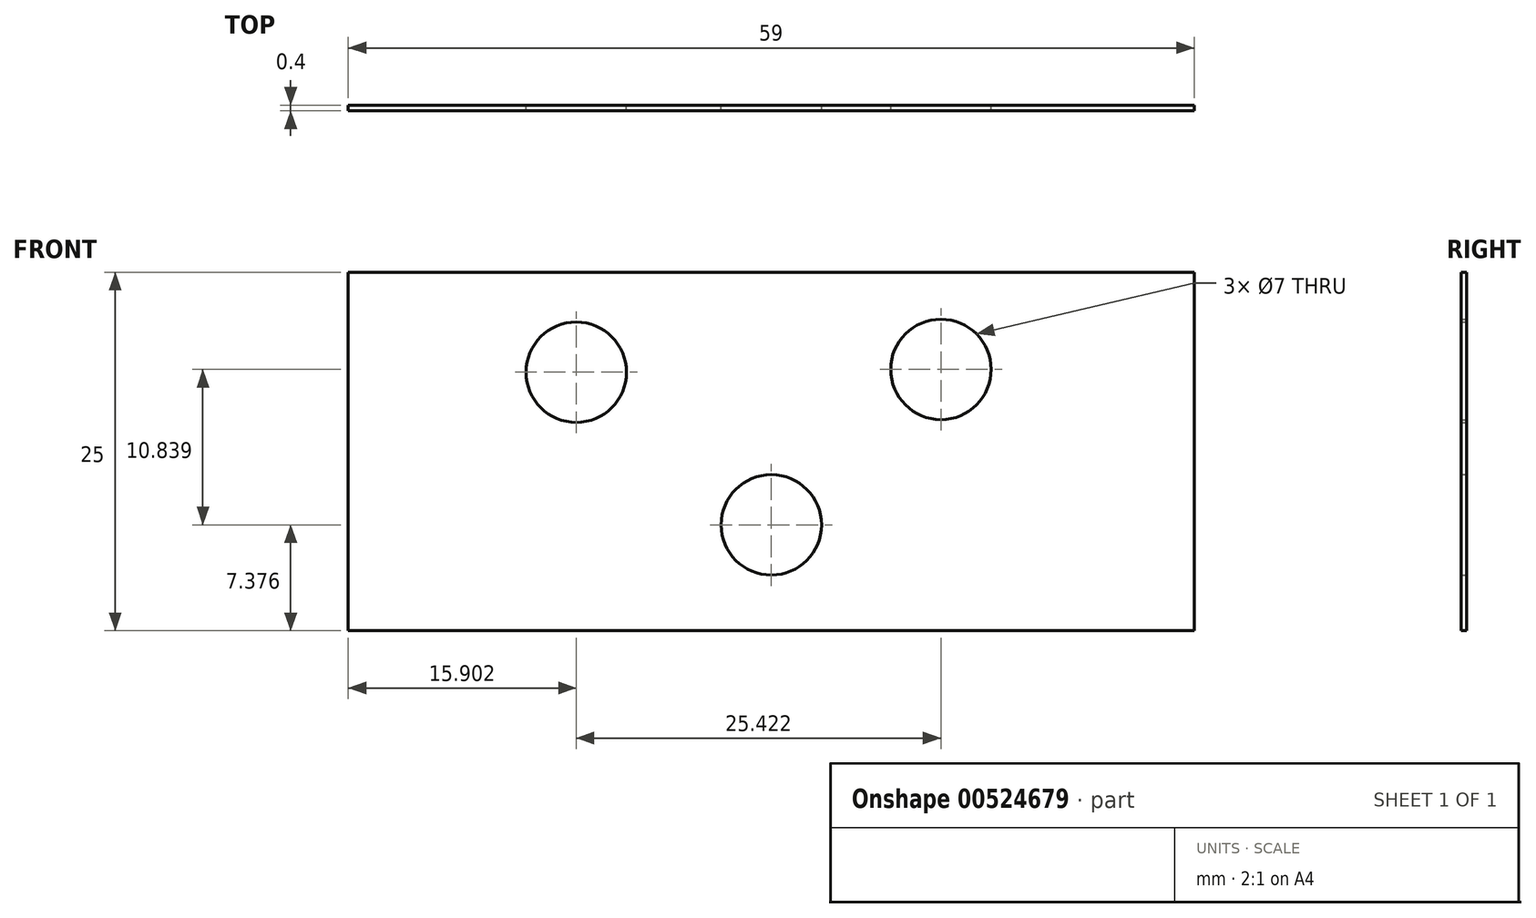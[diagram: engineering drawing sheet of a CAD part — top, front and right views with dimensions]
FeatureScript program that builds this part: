
annotation { "Feature Type Name" : "Feature", "Feature Type Description" : "" }
export const myFeature = defineFeature(function(context is Context, id is Id, definition is map)
    precondition{}
    {
        {
            var Q0;
            Q0=qCreatedBy(makeId("Front.planeOp"),FACE);
            var sketch = newSketch(context, id + "F0", { "sketchPlane" : qUnion([Q0])});
            skLineSegment(sketch, "E0.bottom", {"start": v(-29.5, 12.5) * mm, "end": v(29.5, 12.5) * mm});
            skLineSegment(sketch, "E0.top", {"start": v(-29.5, -12.5) * mm, "end": v(29.5, -12.5) * mm});
            skLineSegment(sketch, "E0.left", {"start": v(-29.5, 12.5) * mm, "end": v(-29.5, -12.5) * mm});
            skLineSegment(sketch, "E0.right", {"start": v(29.5, 12.5) * mm, "end": v(29.5, -12.5) * mm});
            skPoint(sketch, "E0.middle", {"position": v(0, 0) * mm});
            skLineSegment(sketch, "E1.bottom", {"start": v(-19.7, 12.5) * mm, "end": v(-6.7, 12.5) * mm});
            skLineSegment(sketch, "E1.top", {"start": v(-19.7, 22.5) * mm, "end": v(-6.7, 22.5) * mm});
            skLineSegment(sketch, "E1.left", {"start": v(-19.7, 12.5) * mm, "end": v(-19.7, 22.5) * mm});
            skLineSegment(sketch, "E1.right", {"start": v(-6.7, 12.5) * mm, "end": v(-6.7, 22.5) * mm});
            skLineSegment(sketch, "E2.bottom", {"start": v(4.73, 12.5) * mm, "end": v(17.73, 12.5) * mm});
            skLineSegment(sketch, "E2.top", {"start": v(4.73, 22.5) * mm, "end": v(17.73, 22.5) * mm});
            skLineSegment(sketch, "E2.left", {"start": v(4.73, 12.5) * mm, "end": v(4.73, 22.5) * mm});
            skLineSegment(sketch, "E2.right", {"start": v(17.73, 12.5) * mm, "end": v(17.73, 22.5) * mm});
            skCircle(sketch, "E3", {"center": v(-13.6, 5.52) * mm, "radius": 3.5 * mm});
            skCircle(sketch, "E4", {"center": v(11.82, 5.72) * mm, "radius": 3.5 * mm});
            skCircle(sketch, "E5", {"center": v(0, -5.12) * mm, "radius": 3.5 * mm});
            skSolve(sketch);
        }
        {
            var Q0;
            Q0=makeQuery(id+"F0.imprint","IMPRINT",FACE,{"disambiguationData":[TD([[makeQuery(id+"F0.imprint","IMPRINT",EDGE,{"derivedFrom":sQuery(id+"F0.wireOp",EDGE,"E1.bottom")}),1.0]])]});
            var Q1;
            Q1=makeQuery(id+"F0.imprint","IMPRINT",FACE,{"disambiguationData":[TD([[makeQuery(id+"F0.imprint","IMPRINT",EDGE,{"derivedFrom":sQuery(id+"F0.wireOp",EDGE,"E0.top")}),1.0]])]});
            var Q2;
            Q2=makeQuery(id+"F0.imprint","IMPRINT",FACE,{"disambiguationData":[TD([[makeQuery(id+"F0.imprint","IMPRINT",EDGE,{"derivedFrom":sQuery(id+"F0.wireOp",EDGE,"E2.bottom")}),1.0]])]});
            extrude(context, id + "F1", {"entities" : qUnion([Q0, Q1, Q2]), "endBound" : BoundingType.SYMMETRIC, "depth" : 0.4 * mm, "offsetDistance" : 25 * mm});
        }
    });
